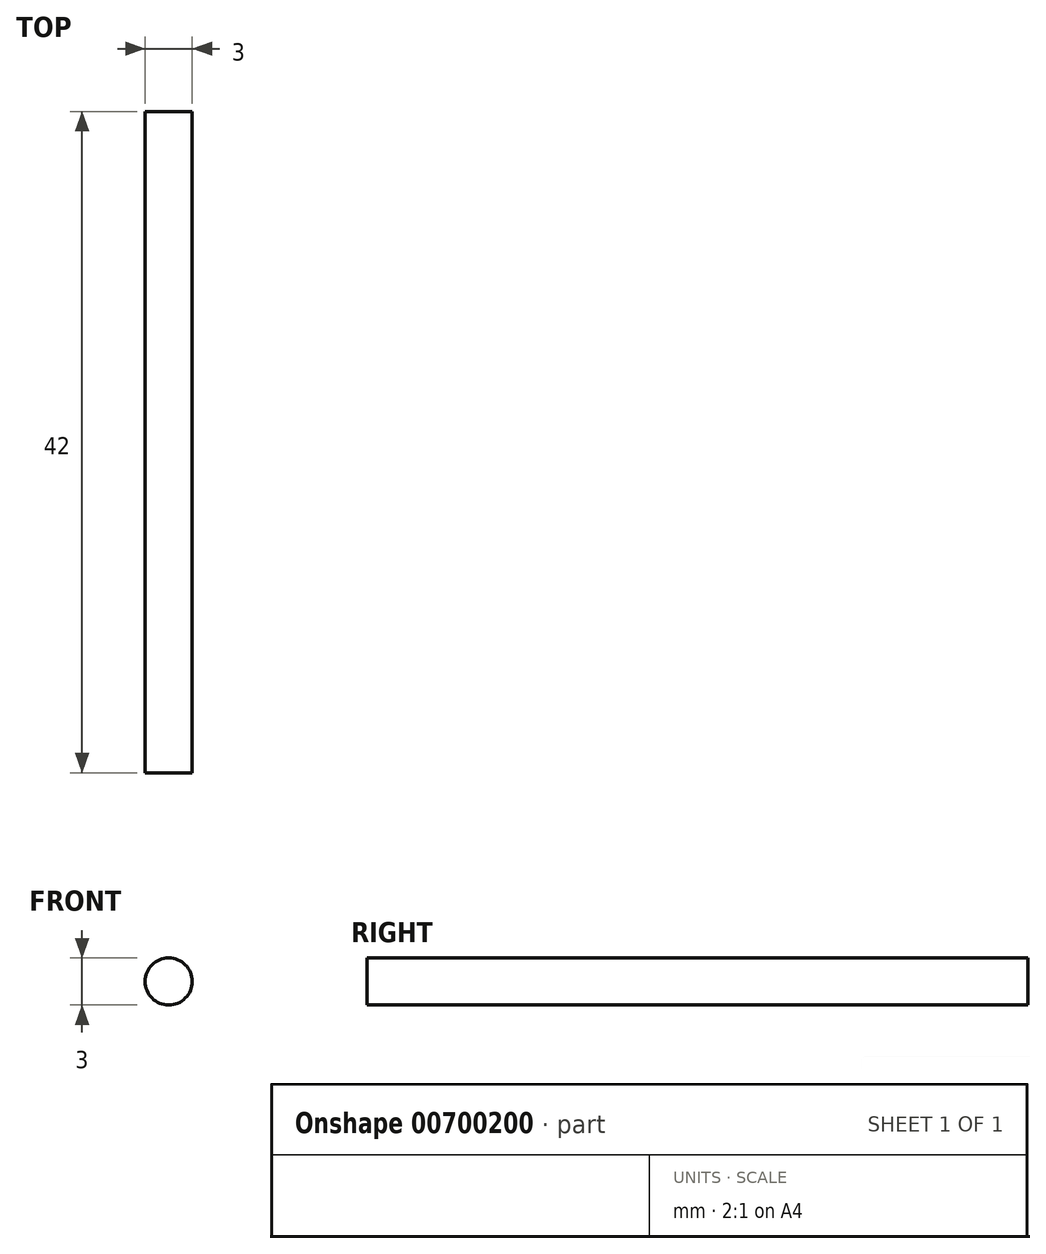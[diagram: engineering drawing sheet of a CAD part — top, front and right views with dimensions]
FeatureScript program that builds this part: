
annotation { "Feature Type Name" : "Feature", "Feature Type Description" : "" }
export const myFeature = defineFeature(function(context is Context, id is Id, definition is map)
    precondition{}
    {
        {
            var Q0;
            Q0=qCreatedBy(makeId("Front.planeOp"),FACE);
            var sketch = newSketch(context, id + "F0", { "sketchPlane" : qUnion([Q0])});
            skCircle(sketch, "E0", {"center": v(0, 0) * mm, "radius": 1.5 * mm});
            skSolve(sketch);
        }
        {
            var Q0;
            Q0=qSketchRegion(id+"F0",true);
            extrude(context, id + "F1", {"entities" : qUnion([Q0]), "depth" : 42 * mm, "offsetDistance" : 25 * mm});
        }
    });
